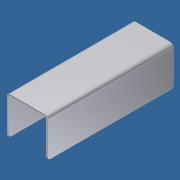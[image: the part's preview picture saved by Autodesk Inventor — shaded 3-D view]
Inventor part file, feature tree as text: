
AUTODESK INVENTOR PART (.ipt)
format: ipt  version: 2012 (Build 160160000, 160)  size: 95,744 bytes
history: native  units: in
note: dims shown in document units (in); Inventor stores cm internally (conversion verified against a paired STEP export)
features: extrude x1, fillet x1, sketch x1
ambient origin geometry x8: Origin, YZ Plane, XZ Plane, XY Plane, X Axis, Y Axis, Z Axis, Center Point
bodies: Solid1 (feature_tree)
feature tree (3):
  extrude  "Extrusion1"  Depth=1.83in
  fillet  "Fillet1"  Radius=6.0in
  sketch  "Sketch1"  dims[d1=0.078in d3=1.83in d4=6.0in d5=0.0in d6=1.8in d7=0.08in d8=0.125in]
